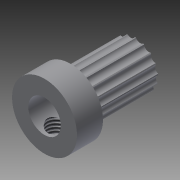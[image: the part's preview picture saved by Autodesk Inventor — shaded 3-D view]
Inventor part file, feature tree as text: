
AUTODESK INVENTOR PART (.ipt)
format: ipt  version: 2013 (Build 170138000, 138)  size: 163,328 bytes
history: native  units: mm
features: sketch x3, extrude x2, revolve x1, thread x1
ambient origin geometry x8: Origin, YZ Plane, XZ Plane, XY Plane, X Axis, Y Axis, Z Axis, Center Point
bodies: Solid1 (feature_tree)
feature tree (7):
  revolve  "Revolution1"  [1 undecoded]
  extrude  "Extrusion1"  Depth=4.0mm
  thread  "Thread1"  [1 undecoded]
  extrude  "Extrusion2"  Depth=2.0mm
  sketch  "Sketch1"  dims[d0=2.5mm d2=3.5mm]
  sketch  "Sketch2"  dims[d3=10.0mm d4=4.0mm d5=5.0mm]
  sketch  "Sketch3"  dims[d6=90.0deg d7=2.0mm d8=3.0mm d9=10.0mm d10=0.0mm d11=10.0mm d12=0.0mm d13=170.0mm d15=360.0deg d17=10.0mm d18=0.0mm]
note: 2 required parameter values undecoded (feature->parameter linkage not recoverable at this tier; creation-order binding heuristic only, values carry confidence <= 0.55)